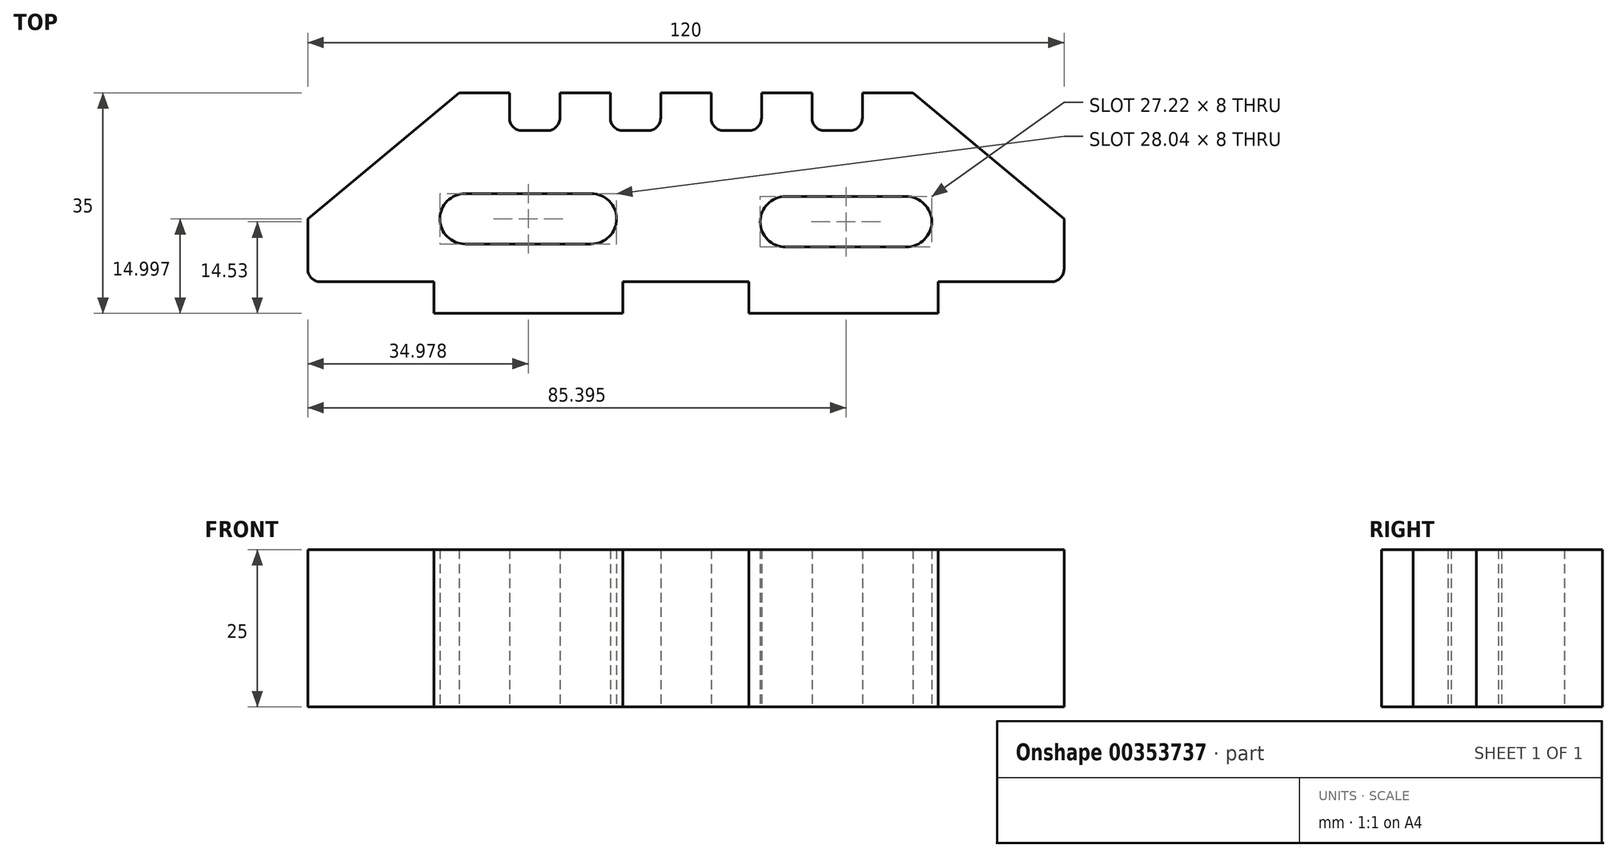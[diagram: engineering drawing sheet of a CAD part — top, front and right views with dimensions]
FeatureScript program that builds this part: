
annotation { "Feature Type Name" : "Feature", "Feature Type Description" : "" }
export const myFeature = defineFeature(function(context is Context, id is Id, definition is map)
    precondition{}
    {
        {
            var Q0;
            Q0=qCreatedBy(makeId("Top.planeOp"),FACE);
            var sketch = newSketch(context, id + "F0", { "sketchPlane" : qUnion([Q0])});
            skLineSegment(sketch, "E0", {"start": v(-48, 10.73) * mm, "end": v(-30, 10.73) * mm});
            skLineSegment(sketch, "E1", {"start": v(-30, 10.73) * mm, "end": v(-30, 5.73) * mm});
            skLineSegment(sketch, "E2", {"start": v(-30, 5.73) * mm, "end": v(0, 5.73) * mm});
            skLineSegment(sketch, "E3", {"start": v(0, 5.73) * mm, "end": v(0, 10.73) * mm});
            skLineSegment(sketch, "E4", {"start": v(0, 10.73) * mm, "end": v(20, 10.73) * mm});
            skLineSegment(sketch, "E5", {"start": v(20, 10.73) * mm, "end": v(20, 5.73) * mm});
            skLineSegment(sketch, "E6", {"start": v(20, 5.73) * mm, "end": v(50, 5.73) * mm});
            skLineSegment(sketch, "E7", {"start": v(50, 5.73) * mm, "end": v(50, 10.73) * mm});
            skLineSegment(sketch, "E8", {"start": v(50, 10.73) * mm, "end": v(68, 10.73) * mm});
            skLineSegment(sketch, "E9", {"start": v(-50, 12.73) * mm, "end": v(-50, 20.73) * mm});
            skLineSegment(sketch, "E10", {"start": v(70, 12.73) * mm, "end": v(70, 20.73) * mm});
            skLineSegment(sketch, "E11", {"start": v(-26, 40.73) * mm, "end": v(-18, 40.73) * mm});
            skLineSegment(sketch, "E12", {"start": v(46, 40.73) * mm, "end": v(38, 40.73) * mm});
            skLineSegment(sketch, "E13", {"start": v(-10, 34.73) * mm, "end": v(-10, 34.73) * mm});
            skLineSegment(sketch, "E14", {"start": v(-10, 36.73) * mm, "end": v(-10, 40.73) * mm});
            skLineSegment(sketch, "E15", {"start": v(-10, 40.73) * mm, "end": v(-2, 40.73) * mm});
            skLineSegment(sketch, "E16", {"start": v(-2, 40.73) * mm, "end": v(-2, 36.73) * mm});
            skLineSegment(sketch, "E17", {"start": v(0, 34.73) * mm, "end": v(4, 34.73) * mm});
            skLineSegment(sketch, "E18", {"start": v(6, 36.73) * mm, "end": v(6, 40.73) * mm});
            skLineSegment(sketch, "E19", {"start": v(6, 40.73) * mm, "end": v(14, 40.73) * mm});
            skLineSegment(sketch, "E20", {"start": v(14, 40.73) * mm, "end": v(14, 36.73) * mm});
            skLineSegment(sketch, "E21", {"start": v(16, 34.73) * mm, "end": v(20, 34.73) * mm});
            skLineSegment(sketch, "E22", {"start": v(22, 36.73) * mm, "end": v(22, 40.73) * mm});
            skLineSegment(sketch, "E23", {"start": v(22, 40.73) * mm, "end": v(30, 40.73) * mm});
            skLineSegment(sketch, "E24", {"start": v(30, 40.73) * mm, "end": v(30, 36.73) * mm});
            skLineSegment(sketch, "E25", {"start": v(32, 34.73) * mm, "end": v(36, 34.73) * mm});
            skLineSegment(sketch, "E26", {"start": v(38, 36.73) * mm, "end": v(38, 40.73) * mm});
            skLineSegment(sketch, "E27", {"start": v(38, 40.73) * mm, "end": v(38, 40.73) * mm});
            skPoint(sketch, "E28.visualSharp", {"position": v(-18, 34.73) * mm});
            skLineSegment(sketch, "E29", {"start": v(-18, 40.73) * mm, "end": v(-18, 36.73) * mm});
            skLineSegment(sketch, "E30", {"start": v(-12, 34.73) * mm, "end": v(-16, 34.73) * mm});
            skArc(sketch, "E31.filletArc", {"start": v(-18, 36.73) * mm, "mid": v(-17.41, 35.31) * mm, "end": v(-16, 34.73) * mm});
            skPoint(sketch, "E32.visualSharp", {"position": v(-10, 34.73) * mm});
            skArc(sketch, "E32.filletArc", {"start": v(-12, 34.73) * mm, "mid": v(-10.59, 35.31) * mm, "end": v(-10, 36.73) * mm});
            skPoint(sketch, "E33.visualSharp", {"position": v(-2, 34.73) * mm});
            skArc(sketch, "E33.filletArc", {"start": v(-2, 36.73) * mm, "mid": v(-1.41, 35.31) * mm, "end": v(0, 34.73) * mm});
            skPoint(sketch, "E34.visualSharp", {"position": v(6, 34.73) * mm});
            skArc(sketch, "E34.filletArc", {"start": v(4, 34.73) * mm, "mid": v(5.41, 35.31) * mm, "end": v(6, 36.73) * mm});
            skPoint(sketch, "E35.visualSharp", {"position": v(14, 34.73) * mm});
            skArc(sketch, "E35.filletArc", {"start": v(14, 36.73) * mm, "mid": v(14.59, 35.31) * mm, "end": v(16, 34.73) * mm});
            skPoint(sketch, "E36.visualSharp", {"position": v(22, 34.73) * mm});
            skArc(sketch, "E36.filletArc", {"start": v(20, 34.73) * mm, "mid": v(21.41, 35.31) * mm, "end": v(22, 36.73) * mm});
            skPoint(sketch, "E37.visualSharp", {"position": v(30, 34.73) * mm});
            skArc(sketch, "E37.filletArc", {"start": v(30, 36.73) * mm, "mid": v(30.59, 35.31) * mm, "end": v(32, 34.73) * mm});
            skPoint(sketch, "E38.visualSharp", {"position": v(38, 34.73) * mm});
            skArc(sketch, "E38.filletArc", {"start": v(36, 34.73) * mm, "mid": v(37.41, 35.31) * mm, "end": v(38, 36.73) * mm});
            skPoint(sketch, "E39.end.orphan", {"position": v(70, 40.73) * mm});
            skLineSegment(sketch, "E40", {"start": v(-50, 20.73) * mm, "end": v(-26, 40.73) * mm});
            skLineSegment(sketch, "E41", {"start": v(70, 20.73) * mm, "end": v(46, 40.73) * mm});
            skPoint(sketch, "E42.visualSharp", {"position": v(-50, 10.73) * mm});
            skArc(sketch, "E42.filletArc", {"start": v(-50, 12.73) * mm, "mid": v(-49.41, 11.31) * mm, "end": v(-48, 10.73) * mm});
            skPoint(sketch, "E43.visualSharp", {"position": v(70, 10.73) * mm});
            skArc(sketch, "E43.filletArc", {"start": v(68, 10.73) * mm, "mid": v(69.41, 11.31) * mm, "end": v(70, 12.73) * mm});
            skLineSegment(sketch, "E44", {"start": v(35, 5.73) * mm, "end": v(35, 20.73) * mm});
            skPoint(sketch, "E45.startSnap0", {"position": v(10, 40.73) * mm});
            skLineSegment(sketch, "E46", {"start": v(49, 20.26) * mm, "end": v(49, 20.26) * mm});
            skLineSegment(sketch, "E47", {"start": v(45, 24.26) * mm, "end": v(25.79, 24.26) * mm});
            skLineSegment(sketch, "E48", {"start": v(45, 16.26) * mm, "end": v(25.79, 16.26) * mm});
            skLineSegment(sketch, "E49", {"start": v(21.79, 20.26) * mm, "end": v(21.79, 20.26) * mm});
            skArc(sketch, "E50.filletArc", {"start": v(25.79, 24.26) * mm, "mid": v(22.96, 23.09) * mm, "end": v(21.79, 20.26) * mm});
            skArc(sketch, "E51.filletArc", {"start": v(21.79, 20.26) * mm, "mid": v(22.96, 17.43) * mm, "end": v(25.79, 16.26) * mm});
            skArc(sketch, "E52.filletArc", {"start": v(49, 20.26) * mm, "mid": v(47.83, 23.09) * mm, "end": v(45, 24.26) * mm});
            skArc(sketch, "E53.filletArc", {"start": v(45, 16.26) * mm, "mid": v(47.83, 17.43) * mm, "end": v(49, 20.26) * mm});
            skPoint(sketch, "E54.end.orphan", {"position": v(-1, 22.97) * mm});
            skPoint(sketch, "E54.start.orphan", {"position": v(10, 22.97) * mm});
            skPoint(sketch, "E55.orphan", {"position": v(-15, 5.73) * mm});
            skPoint(sketch, "E56.start.orphan", {"position": v(-15, 20.73) * mm});
            skLineSegment(sketch, "E57", {"start": v(-1, 20.73) * mm, "end": v(-1, 20.73) * mm});
            skLineSegment(sketch, "E58", {"start": v(-29.04, 20.73) * mm, "end": v(-29.04, 20.73) * mm});
            skLineSegment(sketch, "E59", {"start": v(-5, 24.73) * mm, "end": v(-25.04, 24.73) * mm});
            skLineSegment(sketch, "E60", {"start": v(-25.04, 16.73) * mm, "end": v(-5, 16.73) * mm});
            skPoint(sketch, "E61.visualSharp", {"position": v(-29.04, 24.73) * mm});
            skArc(sketch, "E61.filletArc", {"start": v(-25.04, 24.73) * mm, "mid": v(-27.87, 23.56) * mm, "end": v(-29.04, 20.73) * mm});
            skPoint(sketch, "E62.visualSharp", {"position": v(-29.04, 16.73) * mm});
            skArc(sketch, "E62.filletArc", {"start": v(-29.04, 20.73) * mm, "mid": v(-27.87, 17.9) * mm, "end": v(-25.04, 16.73) * mm});
            skPoint(sketch, "E63.visualSharp", {"position": v(-1, 24.73) * mm});
            skArc(sketch, "E63.filletArc", {"start": v(-1, 20.73) * mm, "mid": v(-2.17, 23.56) * mm, "end": v(-5, 24.73) * mm});
            skPoint(sketch, "E64.visualSharp", {"position": v(-1, 16.73) * mm});
            skArc(sketch, "E64.filletArc", {"start": v(-5, 16.73) * mm, "mid": v(-2.17, 17.9) * mm, "end": v(-1, 20.73) * mm});
            skSolve(sketch);
        }
        {
            var Q0;
            Q0=makeQuery(id+"F0.imprint","IMPRINT",FACE,{"disambiguationData":[TD([[makeQuery(id+"F0.imprint","IMPRINT",EDGE,{"derivedFrom":sQuery(id+"F0.wireOp",EDGE,"E0")}),1.0]])]});
            extrude(context, id + "F1", {"entities" : qUnion([Q0]), "depth" : 25 * mm});
        }
    });
